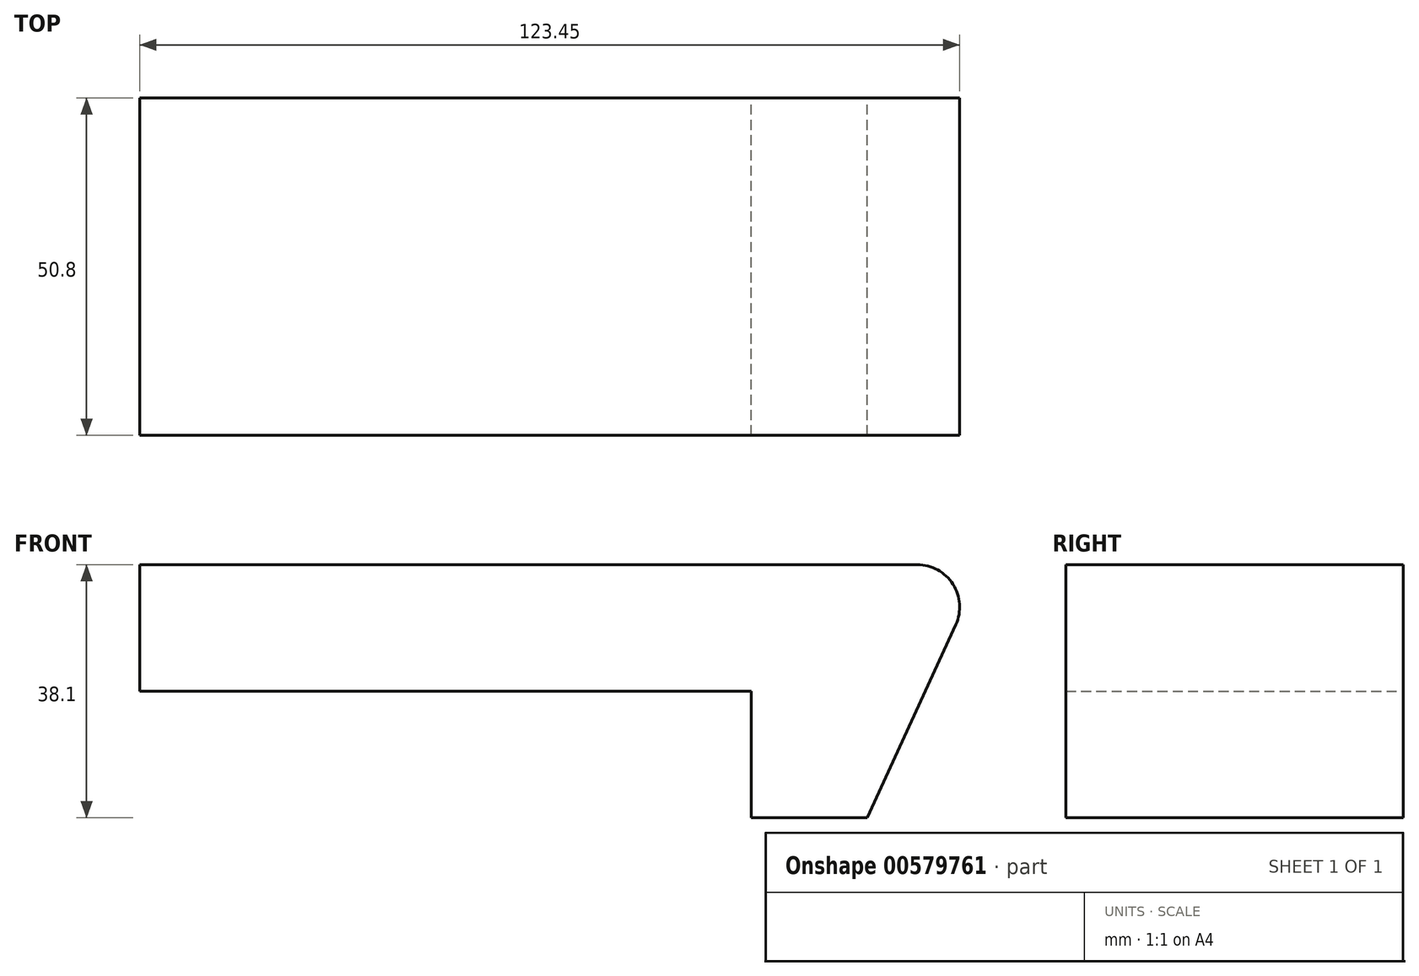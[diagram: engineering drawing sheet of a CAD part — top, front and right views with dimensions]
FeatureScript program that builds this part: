
annotation { "Feature Type Name" : "Feature", "Feature Type Description" : "" }
export const myFeature = defineFeature(function(context is Context, id is Id, definition is map)
    precondition{}
    {
        {
            var Q0;
            Q0=qCreatedBy(makeId("Front.planeOp"),FACE);
            var sketch = newSketch(context, id + "F0", { "sketchPlane" : qUnion([Q0])});
            skLineSegment(sketch, "E0", {"start": v(0, 0) * mm, "end": v(127, 0) * mm});
            skLineSegment(sketch, "E1", {"start": v(92.07, -38.1) * mm, "end": v(92.07, -19.05) * mm});
            skLineSegment(sketch, "E2", {"start": v(92.07, -19.05) * mm, "end": v(0, -19.05) * mm});
            skLineSegment(sketch, "E3", {"start": v(0, -19.05) * mm, "end": v(0, 0) * mm});
            skLineSegment(sketch, "E4", {"start": v(109.54, -38.1) * mm, "end": v(127, 0) * mm});
            skLineSegment(sketch, "E5", {"start": v(92.07, -38.1) * mm, "end": v(109.54, -38.1) * mm});
            skSolve(sketch);
        }
        {
            var Q0;
            Q0 = qSketchRegion(id + "F0", true);
            var Q1;
            Q1=makeQuery(id+"F0.imprint","IMPRINT",FACE,{"disambiguationData":[TD([[makeQuery(id+"F0.imprint","IMPRINT",EDGE,{"derivedFrom":sQuery(id+"F0.wireOp",EDGE,"E0")}),-1.0]])]});
            extrude(context, id + "F1", {"entities" : qUnion([Q0, Q1]), "flatOperationType" : FlatOperationType.REMOVE, "depth" : 50.8 * mm, "offsetDistance" : 25.4 * mm, "domain" : OperationDomain.MODEL});
        }
        {
            var Q0;
            Q0=makeQuery(id+"F1.opExtrude","SWEPT_EDGE",EDGE,{"disambiguationData":[OSD([sQuery(id+"F0.wireOp",EDGE,"E0"),sQuery(id+"F0.wireOp",EDGE,"E4")])]});
            fillet(context, id + "F2", {"entities" : qUnion([Q0]), "radius" : 6.35 * mm, "tangentPropagation" : true, "defaultsChanged" : true, "vertexSettings" : [], "allowEdgeOverflow" : false});
        }
    });
